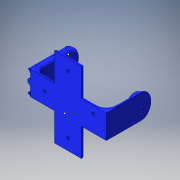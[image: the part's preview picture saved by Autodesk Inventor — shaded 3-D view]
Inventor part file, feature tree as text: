
AUTODESK INVENTOR PART (.ipt)
format: ipt  version: 2016 (Build 200138000, 138)  size: 568,832 bytes
history: native  units: in
note: dims shown in document units (in); Inventor stores cm internally (conversion verified against a paired STEP export)
features: sketch x13, other x3
ambient origin geometry x8: Origin, YZ Plane, XZ Plane, XY Plane, X Axis, Y Axis, Z Axis, Center Point
bodies: Solid1 (feature_tree)
feature tree (16):
  other  "Hip_forward_v2.ipt"
  other  "Solid1::Hip_forward_v2.ipt"
  other  "TaggingFeature1"
  sketch  "Sketch1"  dims[d0=0.3937in]
  sketch  "Sketch4"
  sketch  "Sketch5"
  sketch  "Sketch7"
  sketch  "Sketch9"
  sketch  "Sketch10"
  sketch  "Sketch15"
  sketch  "Sketch16"
  sketch  "Sketch17"
  sketch  "Sketch18"
  sketch  "Sketch19"
  sketch  "Sketch20"
  sketch  "Sketch21"
